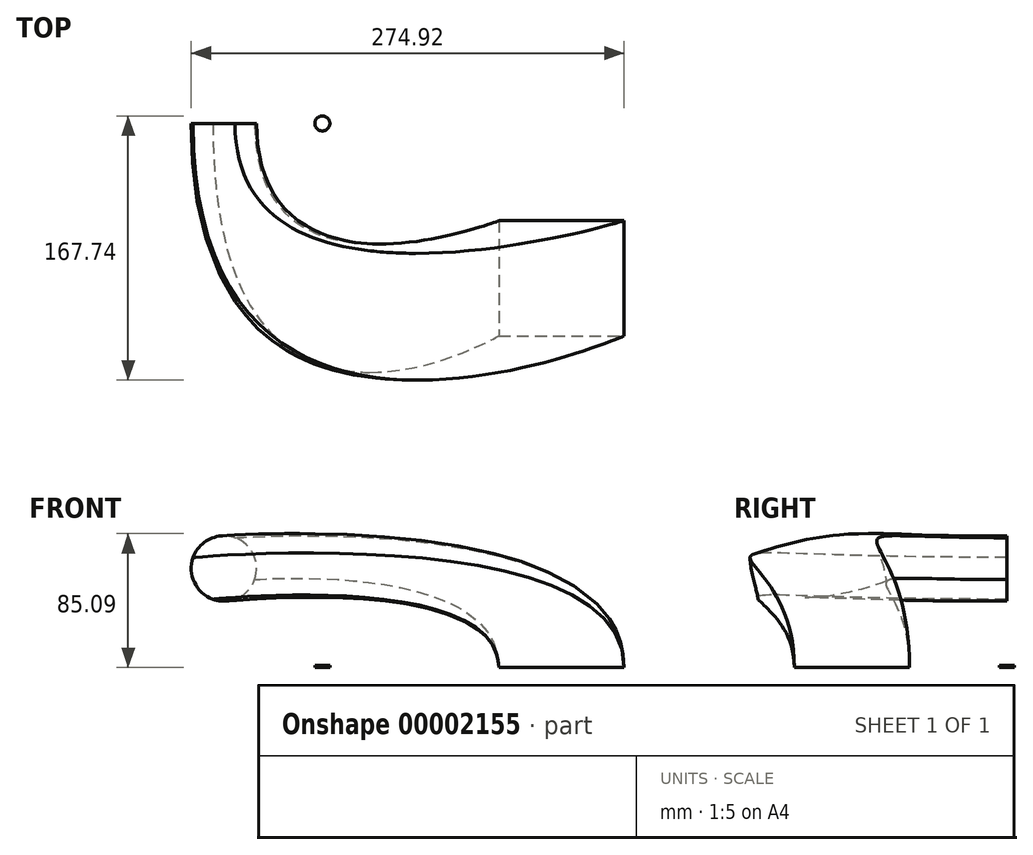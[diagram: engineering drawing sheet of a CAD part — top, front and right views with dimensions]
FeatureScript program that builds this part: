
annotation { "Feature Type Name" : "Feature", "Feature Type Description" : "" }
export const myFeature = defineFeature(function(context is Context, id is Id, definition is map)
    precondition{}
    {
        {
            var Q0;
            Q0=qCreatedBy(makeId("Top.planeOp"),FACE);
            var sketch = newSketch(context, id + "F0", { "sketchPlane" : qUnion([Q0])});
            skCircle(sketch, "E0", {"center": v(0, 0) * mm, "radius": 4.76 * mm});
            skSolve(sketch);
        }
        {
            var Q0;
            Q0 = qSketchRegion(id + "F0", true);
            extrude(context, id + "F1", {"entities" : qUnion([Q0]), "depth" : 1.27 * mm});
        }
        {
            var Q0;
            Q0=qCreatedBy(makeId("Front.planeOp"),FACE);
            var sketch = newSketch(context, id + "F2", { "sketchPlane" : qUnion([Q0])});
            skCircle(sketch, "E1", {"center": v(-62.5, 62.9) * mm, "radius": 20.75 * mm});
            skSolve(sketch);
        }
        {
            var Q0;
            Q0=qCreatedBy(makeId("Top.planeOp"),FACE);
            var sketch = newSketch(context, id + "F3", { "sketchPlane" : qUnion([Q0])});
            skLineSegment(sketch, "E2.bottom", {"start": v(112.08, -61.77) * mm, "end": v(191.66, -61.77) * mm});
            skLineSegment(sketch, "E2.top", {"start": v(112.08, -134.9) * mm, "end": v(191.66, -134.9) * mm});
            skLineSegment(sketch, "E2.left", {"start": v(112.08, -61.77) * mm, "end": v(112.08, -134.9) * mm});
            skLineSegment(sketch, "E2.right", {"start": v(191.66, -61.77) * mm, "end": v(191.66, -134.9) * mm});
            skSolve(sketch);
        }
        {
            var Q0;
            Q0=makeQuery(id+"F2.imprint","IMPRINT",FACE,{"disambiguationData":[TD([[makeQuery(id+"F2.imprint","IMPRINT",EDGE,{"derivedFrom":sQuery(id+"F2.wireOp",EDGE,"E1")}),1.0]])]});
            var Q1;
            Q1=makeQuery(id+"F3.imprint","IMPRINT",FACE,{"disambiguationData":[TD([[makeQuery(id+"F3.imprint","IMPRINT",EDGE,{"derivedFrom":sQuery(id+"F3.wireOp",EDGE,"E2.bottom")}),-1.0]])]});
            loft(context, id + "F4", {"sheetProfilesArray" : [{ "sheetProfileEntities" : qUnion([Q0]) }, { "sheetProfileEntities" : qUnion([Q1]) }], "startCondition" : LoftEndDerivativeType.NORMAL_TO_PROFILE, "startMagnitude" : 5, "endCondition" : LoftEndDerivativeType.NORMAL_TO_PROFILE, "endMagnitude" : 3});
        }
    });
